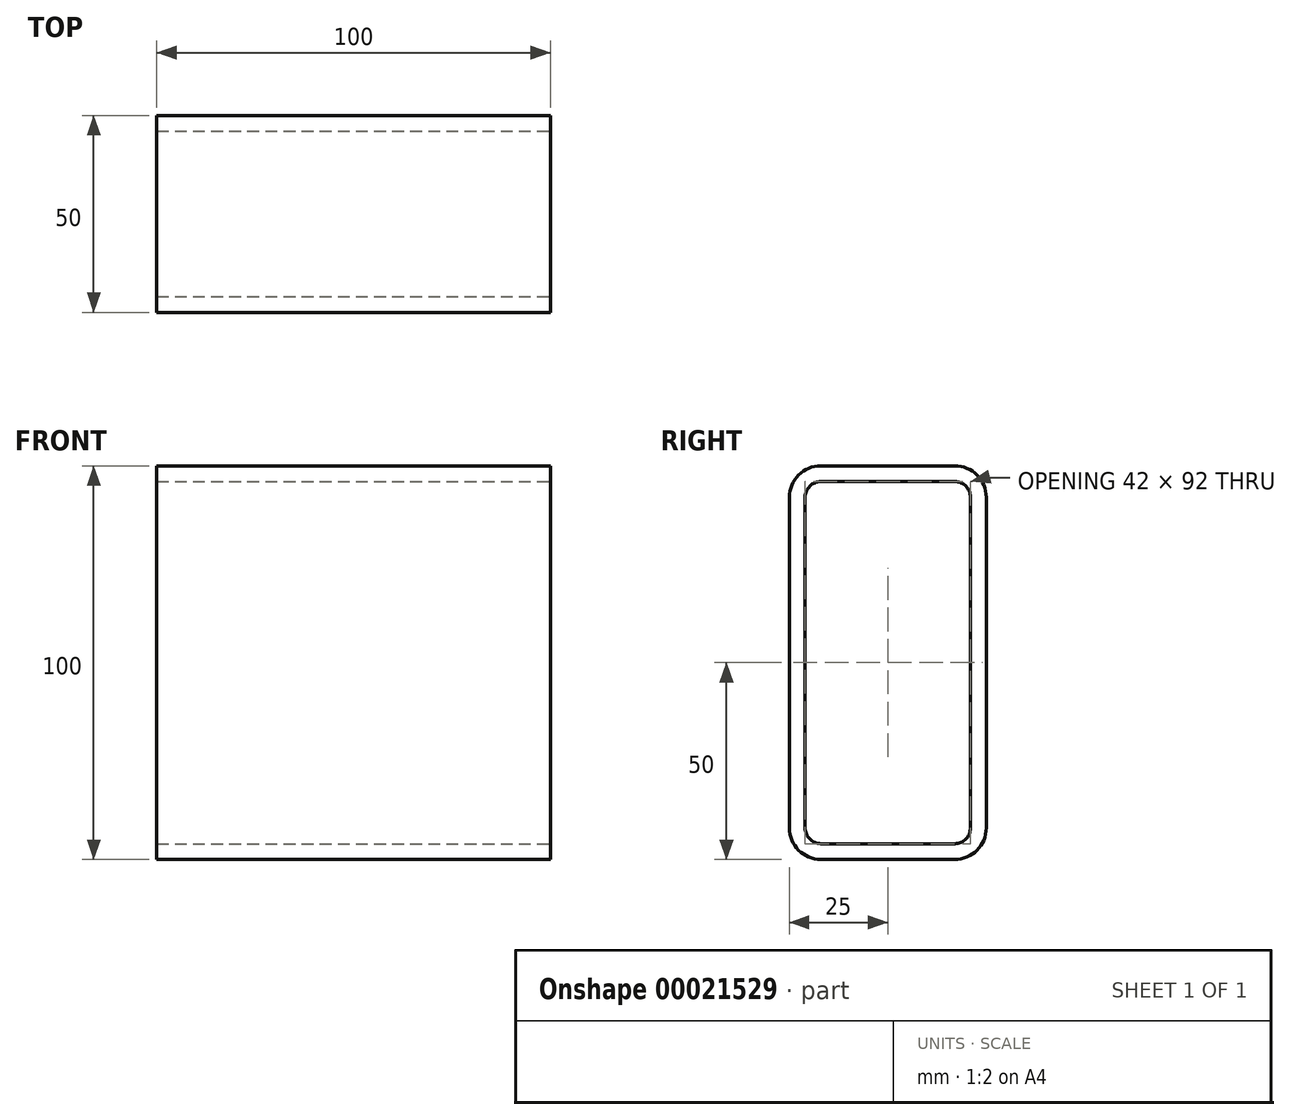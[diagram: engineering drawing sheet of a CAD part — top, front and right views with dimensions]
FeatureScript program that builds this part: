
annotation { "Feature Type Name" : "Feature", "Feature Type Description" : "" }
export const myFeature = defineFeature(function(context is Context, id is Id, definition is map)
    precondition{}
    {
        {
            var Q0;
            Q0=qCreatedBy(makeId("Right.planeOp"),FACE);
            var sketch = newSketch(context, id + "F0", { "sketchPlane" : qUnion([Q0])});
            skLineSegment(sketch, "E0.bottom", {"start": v(8, 0) * mm, "end": v(42, 0) * mm});
            skLineSegment(sketch, "E0.top", {"start": v(8, 100) * mm, "end": v(42, 100) * mm});
            skLineSegment(sketch, "E0.left", {"start": v(0, 8) * mm, "end": v(0, 92) * mm});
            skLineSegment(sketch, "E0.right", {"start": v(50, 8) * mm, "end": v(50, 92) * mm});
            skPoint(sketch, "E1.visualSharp", {"position": v(0, 100) * mm});
            skArc(sketch, "E1.filletArc", {"start": v(8, 100) * mm, "mid": v(2.34, 97.66) * mm, "end": v(0, 92) * mm});
            skPoint(sketch, "E2.visualSharp", {"position": v(50, 100) * mm});
            skArc(sketch, "E2.filletArc", {"start": v(50, 92) * mm, "mid": v(47.66, 97.66) * mm, "end": v(42, 100) * mm});
            skPoint(sketch, "E3.visualSharp", {"position": v(50, 0) * mm});
            skArc(sketch, "E3.filletArc", {"start": v(42, 0) * mm, "mid": v(47.66, 2.34) * mm, "end": v(50, 8) * mm});
            skPoint(sketch, "E4.visualSharp", {"position": v(0, 0) * mm});
            skArc(sketch, "E4.filletArc", {"start": v(0, 8) * mm, "mid": v(2.34, 2.34) * mm, "end": v(8, 0) * mm});
            skLineSegment(sketch, "E5.0", {"start": v(46, 8) * mm, "end": v(46, 92) * mm});
            skArc(sketch, "E6.0", {"start": v(46, 92) * mm, "mid": v(44.83, 94.83) * mm, "end": v(42, 96) * mm});
            skLineSegment(sketch, "E7.0", {"start": v(8, 96) * mm, "end": v(42, 96) * mm});
            skArc(sketch, "E7.1", {"start": v(8, 96) * mm, "mid": v(5.17, 94.83) * mm, "end": v(4, 92) * mm});
            skArc(sketch, "E7.2", {"start": v(42, 4) * mm, "mid": v(44.83, 5.17) * mm, "end": v(46, 8) * mm});
            skLineSegment(sketch, "E7.3", {"start": v(8, 4) * mm, "end": v(42, 4) * mm});
            skArc(sketch, "E7.4", {"start": v(4, 8) * mm, "mid": v(5.17, 5.17) * mm, "end": v(8, 4) * mm});
            skLineSegment(sketch, "E7.5", {"start": v(4, 8) * mm, "end": v(4, 92) * mm});
            skSolve(sketch);
        }
        {
            var Q0;
            Q0 = qSketchRegion(id + "F0", true);
            var Q1;
            Q1 = qBodyType(qCreatedBy(id + "F0" ,EDGE), BodyType.WIRE);
            extrude(context, id + "F1", {"entities" : qUnion([Q0]), "surfaceEntities" : qUnion([Q1]), "endBound" : BoundingType.SYMMETRIC, "oppositeDirection" : true, "depth" : 100 * mm});
        }
    });
